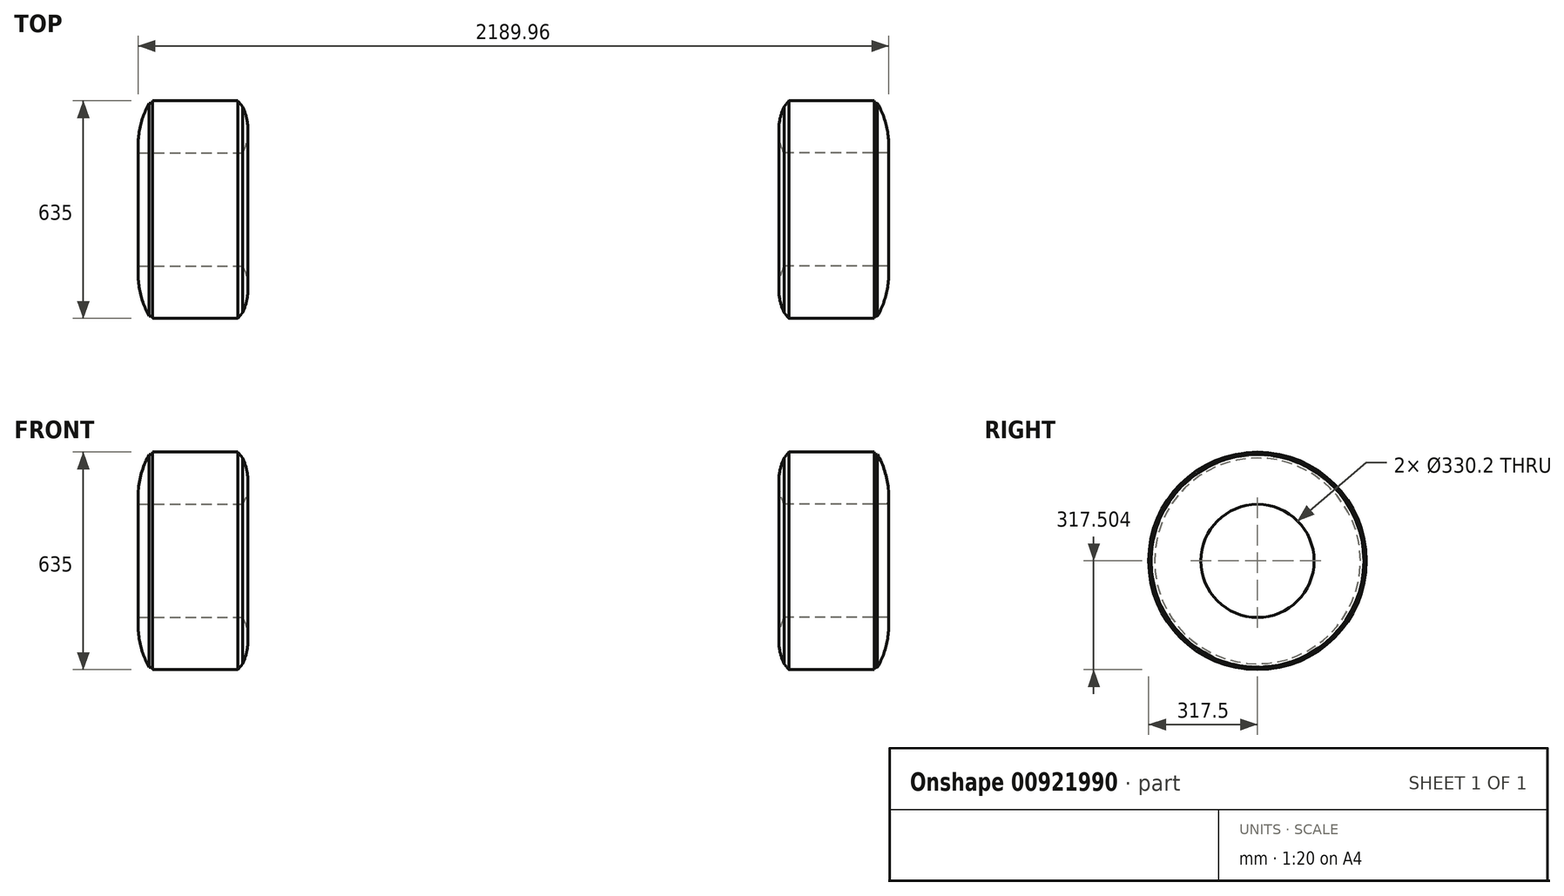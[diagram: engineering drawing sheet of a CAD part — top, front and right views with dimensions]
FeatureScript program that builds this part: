
annotation { "Feature Type Name" : "Feature", "Feature Type Description" : "" }
export const myFeature = defineFeature(function(context is Context, id is Id, definition is map)
    precondition{}
    {
        {
            var Q0;
            Q0=qCreatedBy(makeId("Front.planeOp"),FACE);
            cPlane(context, id + "F0", {"entities" : qUnion([Q0]), "cplaneType" : CPlaneType.OFFSET, "offset" : 1120 * mm, "width" : 150 * mm, "height" : 150 * mm});
        }
        {
            var Q0;
            Q0=qCreatedBy(id+"F0.planeOp",FACE);
            var sketch = newSketch(context, id + "F1", { "sketchPlane" : qUnion([Q0])});
            skLineSegment(sketch, "E0", {"start": v(304, 282.27) * mm, "end": v(1511.42, 282.27) * mm});
            skLineSegment(sketch, "E1", {"start": v(789.2, 447.37) * mm, "end": v(1094, 447.37) * mm});
            skArc(sketch, "E2", {"start": v(790.1, 582.4) * mm, "mid": v(796.74, 591.33) * mm, "end": v(803.98, 599.77) * mm});
            skArc(sketch, "E3", {"start": v(1062.37, 592.54) * mm, "mid": v(1089.27, 522.37) * mm, "end": v(1094, 447.37) * mm});
            skArc(sketch, "E4", {"start": v(790.1, 582.4) * mm, "mid": v(774.3, 515) * mm, "end": v(789.2, 447.37) * mm});
            skArc(sketch, "E5", {"start": v(1052.42, 599.77) * mm, "mid": v(1055.78, 593.93) * mm, "end": v(1062.37, 592.54) * mm});
            skLineSegment(sketch, "E6", {"start": v(803.98, 599.77) * mm, "end": v(1052.42, 599.77) * mm});
            skSolve(sketch);
        }
        {
            var Q0;
            Q0=makeQuery(id+"F1.imprint","IMPRINT",FACE,{"disambiguationData":[TD([[makeQuery(id+"F1.imprint","IMPRINT",EDGE,{"derivedFrom":sQuery(id+"F1.wireOp",EDGE,"E1")}),1.0]])]});
            var Q1;
            Q1=sQuery(id+"F1.wireOp",EDGE,"E0");
            revolve(context, id + "F2", {"surfaceOperationType" : NewSurfaceOperationType.NEW, "entities" : qUnion([Q0]), "axis" : qUnion([Q1]), "revolveType" : RevolveType.FULL});
        }
        {
            var Q0;
            Q0=makeQuery(id+"F2.opRevolve","SWEPT_BODY",BODY,{"disambiguationData":[OSD([sQuery(id+"F1.wireOp",EDGE,"LFTGXg79-ETJX-uzfP-g4PQ-aJrpYjON7s84"),sQuery(id+"F1.wireOp",EDGE,"E1"),sQuery(id+"F1.wireOp",EDGE,"E2"),sQuery(id+"F1.wireOp",EDGE,"E3"),sQuery(id+"F1.wireOp",EDGE,"E4"),sQuery(id+"F1.wireOp",EDGE,"E5")])]});
            var Q1;
            Q1=qCreatedBy(makeId("Right.planeOp"),FACE);
            mirror(context, id + "F3", {"entities" : qUnion([Q0]), "mirrorPlane" : qUnion([Q1])});
        }
    });
